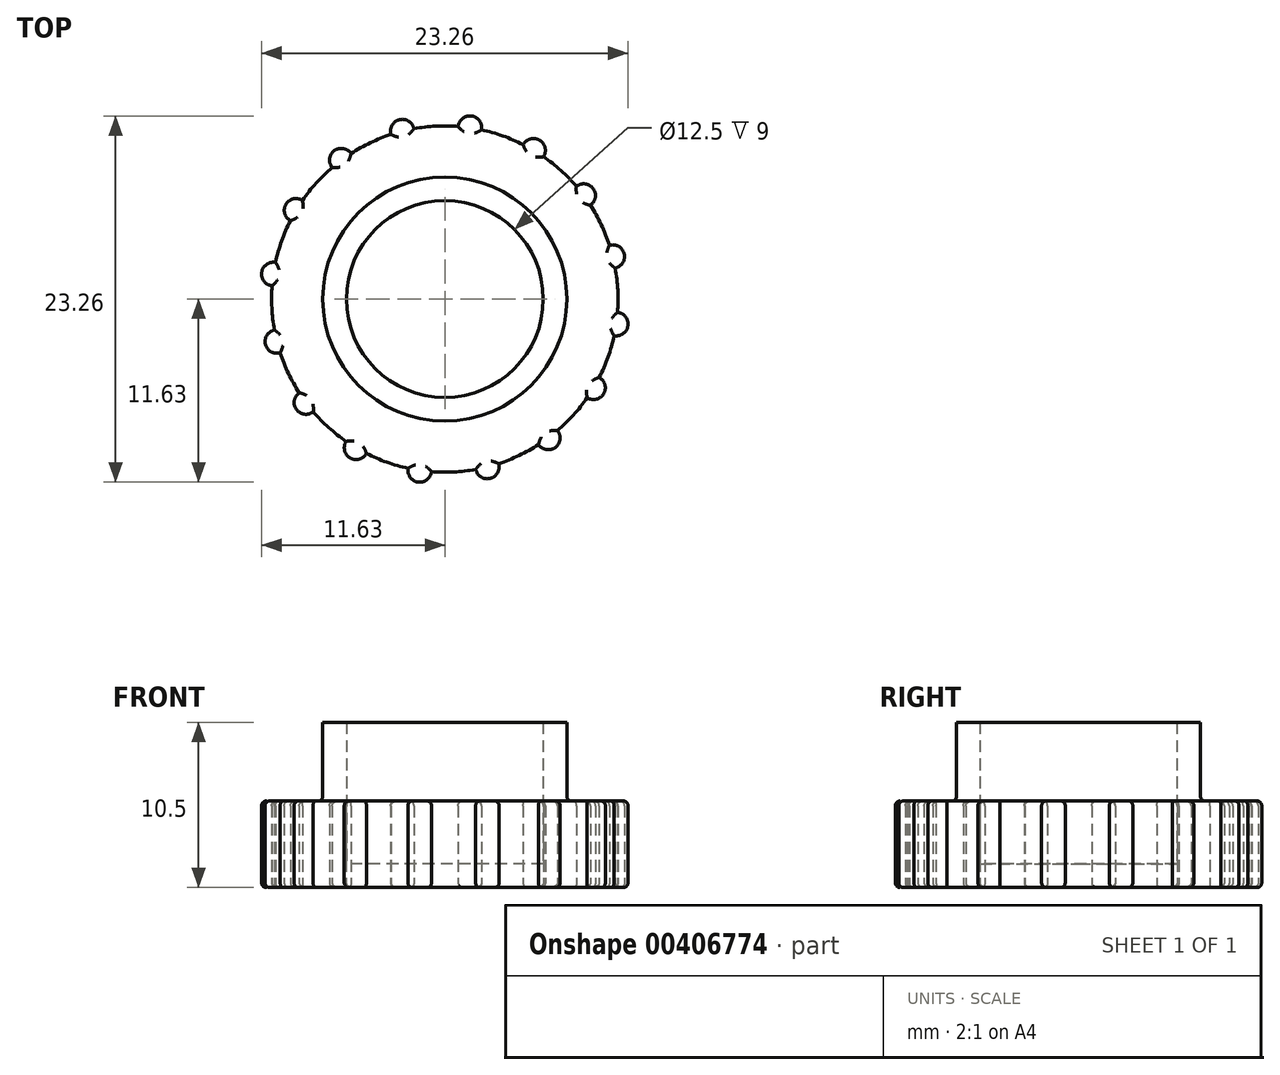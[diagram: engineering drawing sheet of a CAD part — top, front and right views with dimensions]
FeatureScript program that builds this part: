
annotation { "Feature Type Name" : "Feature", "Feature Type Description" : "" }
export const myFeature = defineFeature(function(context is Context, id is Id, definition is map)
    precondition{}
    {
        {
            var Q0;
            Q0=qCreatedBy(makeId("Top.planeOp"),FACE);
            var sketch = newSketch(context, id + "F0", { "sketchPlane" : qUnion([Q0])});
            skCircle(sketch, "E0", {"center": v(0, 0) * mm, "radius": 6.25 * mm});
            skCircle(sketch, "E1", {"center": v(0, 0) * mm, "radius": 7.75 * mm});
            skCircle(sketch, "E2", {"center": v(0, 0) * mm, "radius": 11 * mm});
            skSolve(sketch);
        }
        {
            var Q0;
            Q0=makeQuery(id+"F0.imprint","IMPRINT",FACE,{"disambiguationData":[TD([[makeQuery(id+"F0.imprint","IMPRINT",EDGE,{"derivedFrom":sQuery(id+"F0.wireOp",EDGE,"E0")}),-1.0]])]});
            extrude(context, id + "F1", {"entities" : qUnion([Q0]), "depth" : 9 * mm});
        }
        {
            var Q0;
            Q0=makeQuery(id+"F0.imprint","IMPRINT",FACE,{"disambiguationData":[TD([[makeQuery(id+"F0.imprint","IMPRINT",EDGE,{"derivedFrom":sQuery(id+"F0.wireOp",EDGE,"E1")}),-1.0]])]});
            extrude(context, id + "F2", {"entities" : qUnion([Q0]), "operationType" : NewBodyOperationType.ADD, "depth" : 4 * mm});
        }
        {
            var Q0;
            Q0=makeQuery(id+"F0.imprint","IMPRINT",FACE,{"disambiguationData":[TD([[makeQuery(id+"F0.imprint","IMPRINT",EDGE,{"derivedFrom":sQuery(id+"F0.wireOp",EDGE,"E1")}),-1.0]])]});
            var Q1;
            Q1=makeQuery(id+"F0.imprint","IMPRINT",FACE,{"disambiguationData":[TD([[makeQuery(id+"F0.imprint","IMPRINT",EDGE,{"derivedFrom":sQuery(id+"F0.wireOp",EDGE,"E0")}),-1.0]])]});
            var Q2;
            Q2=makeQuery(id+"F0.imprint","IMPRINT",FACE,{"disambiguationData":[TD([[makeQuery(id+"F0.imprint","IMPRINT",EDGE,{"derivedFrom":sQuery(id+"F0.wireOp",EDGE,"E0")}),1.0]])]});
            extrude(context, id + "F3", {"entities" : qUnion([Q0, Q1, Q2]), "operationType" : NewBodyOperationType.ADD, "oppositeDirection" : true, "depth" : 1.5 * mm});
        }
        {
            var Q0;
            Q0=makeQuery(id+"F3.opExtrude","CAP_FACE",FACE,{"disambiguationData":[OSD([sQuery(id+"F0.wireOp",EDGE,"E2")])],"isStart":false});
            var sketch = newSketch(context, id + "F4", { "sketchPlane" : qUnion([Q0])});
            skCircle(sketch, "E3", {"center": v(-1.6, 10.88) * mm, "radius": 0.75 * mm});
            skSolve(sketch);
        }
        {
            var Q0;
            Q0 = qSketchRegion(id + "F4", true);
            extrude(context, id + "F5", {"entities" : qUnion([Q0]), "oppositeDirection" : true, "depth" : 5.5 * mm});
        }
        {
            var Q0;
            Q0=makeQuery(id+"F5.opExtrude","SWEPT_BODY",BODY,{"disambiguationData":[OSD([sQuery(id+"F4.wireOp",EDGE,"E3")])]});
            var Q1;
            {var subQ0=sQuery(id+"F0.wireOp",EDGE,"E2");Q1=makeQuery(id+"F3.boolean.opBoolean","MERGE",FACE,{"derivedFrom":[makeQuery(id+"F2.opExtrude","SWEPT_FACE",FACE,{"disambiguationData":[OSD([subQ0])]}),makeQuery(id+"F3.opExtrude","SWEPT_FACE",FACE,{"disambiguationData":[OSD([subQ0])]})]});}
            circularPattern(context, id + "F6", {"operationType" : NewBodyOperationType.ADD, "entities" : qUnion([Q0]), "axis" : qUnion([Q1]), "angle" : 360 * degree, "instanceCount" : 16, "equalSpace" : true});
        }
        {
            var Q0;
            Q0=makeQuery(id+"F6.opPattern","COPY",EDGE,{"derivedFrom":makeQuery(id+"F5.opExtrude","CAP_EDGE",EDGE,{"disambiguationData":[OSD([sQuery(id+"F4.wireOp",EDGE,"E3")])],"isStart":true}),"instanceName":"9"});
            var Q1;
            {var subQ0=sQuery(id+"F4.wireOp",EDGE,"E3");var subQ1=makeQuery(id+"F5.opExtrude","CAP_FACE",FACE,{"disambiguationData":[OSD([subQ0])],"isStart":true});var subQ2=sQuery(id+"F0.wireOp",EDGE,"E2");var subQ3=makeQuery(id+"F5.opExtrude","SWEPT_FACE",FACE,{"disambiguationData":[OSD([subQ0])]});Q1=makeQuery(id+"F6.boolean.opBoolean","SPLIT",EDGE,{"disambiguationData":[TD([makeQuery(id+"F2.opExtrude","SWEPT_FACE",FACE,{"disambiguationData":[OSD([subQ2])]}),makeQuery(id+"F3.opExtrude","SWEPT_FACE",FACE,{"disambiguationData":[OSD([subQ2])]}),makeQuery(id+"F3.opExtrude","CAP_FACE",FACE,{"disambiguationData":[OSD([subQ2])],"isStart":false}),subQ1,makeQuery(id+"F6.opPattern","COPY",FACE,{"derivedFrom":subQ1,"instanceName":"1"}),makeQuery(id+"F6.opPattern","COPY",FACE,{"derivedFrom":subQ1,"instanceName":"2"}),makeQuery(id+"F6.opPattern","COPY",FACE,{"derivedFrom":subQ1,"instanceName":"3"}),makeQuery(id+"F6.opPattern","COPY",FACE,{"derivedFrom":subQ1,"instanceName":"4"}),makeQuery(id+"F6.opPattern","COPY",FACE,{"derivedFrom":subQ1,"instanceName":"5"}),makeQuery(id+"F6.opPattern","COPY",FACE,{"derivedFrom":subQ1,"instanceName":"6"}),makeQuery(id+"F6.opPattern","COPY",FACE,{"derivedFrom":subQ1,"instanceName":"7"}),makeQuery(id+"F6.opPattern","COPY",FACE,{"derivedFrom":subQ3,"instanceName":"8"}),makeQuery(id+"F6.opPattern","COPY",FACE,{"derivedFrom":subQ1,"instanceName":"8"}),makeQuery(id+"F6.opPattern","COPY",FACE,{"derivedFrom":subQ3,"instanceName":"9"}),makeQuery(id+"F6.opPattern","COPY",FACE,{"derivedFrom":subQ1,"instanceName":"9"}),makeQuery(id+"F6.opPattern","COPY",FACE,{"derivedFrom":subQ1,"instanceName":"10"}),makeQuery(id+"F6.opPattern","COPY",FACE,{"derivedFrom":subQ1,"instanceName":"11"}),makeQuery(id+"F6.opPattern","COPY",FACE,{"derivedFrom":subQ1,"instanceName":"12"}),makeQuery(id+"F6.opPattern","COPY",FACE,{"derivedFrom":subQ1,"instanceName":"13"}),makeQuery(id+"F6.opPattern","COPY",FACE,{"derivedFrom":subQ1,"instanceName":"14"}),makeQuery(id+"F6.opPattern","COPY",FACE,{"derivedFrom":subQ1,"instanceName":"15"})])],"derivedFrom":makeQuery(id+"F3.opExtrude","CAP_EDGE",EDGE,{"disambiguationData":[OSD([subQ2])],"isStart":false})});}
            var Q2;
            Q2=makeQuery(id+"F6.opPattern","COPY",EDGE,{"derivedFrom":makeQuery(id+"F5.opExtrude","CAP_EDGE",EDGE,{"disambiguationData":[OSD([sQuery(id+"F4.wireOp",EDGE,"E3")])],"isStart":true}),"instanceName":"8"});
            var Q3;
            {var subQ0=sQuery(id+"F4.wireOp",EDGE,"E3");var subQ1=makeQuery(id+"F5.opExtrude","CAP_FACE",FACE,{"disambiguationData":[OSD([subQ0])],"isStart":true});var subQ2=sQuery(id+"F0.wireOp",EDGE,"E2");var subQ3=makeQuery(id+"F5.opExtrude","SWEPT_FACE",FACE,{"disambiguationData":[OSD([subQ0])]});Q3=makeQuery(id+"F6.boolean.opBoolean","SPLIT",EDGE,{"disambiguationData":[TD([makeQuery(id+"F2.opExtrude","SWEPT_FACE",FACE,{"disambiguationData":[OSD([subQ2])]}),makeQuery(id+"F3.opExtrude","SWEPT_FACE",FACE,{"disambiguationData":[OSD([subQ2])]}),makeQuery(id+"F3.opExtrude","CAP_FACE",FACE,{"disambiguationData":[OSD([subQ2])],"isStart":false}),subQ1,makeQuery(id+"F6.opPattern","COPY",FACE,{"derivedFrom":subQ1,"instanceName":"1"}),makeQuery(id+"F6.opPattern","COPY",FACE,{"derivedFrom":subQ1,"instanceName":"2"}),makeQuery(id+"F6.opPattern","COPY",FACE,{"derivedFrom":subQ1,"instanceName":"3"}),makeQuery(id+"F6.opPattern","COPY",FACE,{"derivedFrom":subQ1,"instanceName":"4"}),makeQuery(id+"F6.opPattern","COPY",FACE,{"derivedFrom":subQ1,"instanceName":"5"}),makeQuery(id+"F6.opPattern","COPY",FACE,{"derivedFrom":subQ1,"instanceName":"6"}),makeQuery(id+"F6.opPattern","COPY",FACE,{"derivedFrom":subQ3,"instanceName":"7"}),makeQuery(id+"F6.opPattern","COPY",FACE,{"derivedFrom":subQ1,"instanceName":"7"}),makeQuery(id+"F6.opPattern","COPY",FACE,{"derivedFrom":subQ3,"instanceName":"8"}),makeQuery(id+"F6.opPattern","COPY",FACE,{"derivedFrom":subQ1,"instanceName":"8"}),makeQuery(id+"F6.opPattern","COPY",FACE,{"derivedFrom":subQ1,"instanceName":"9"}),makeQuery(id+"F6.opPattern","COPY",FACE,{"derivedFrom":subQ1,"instanceName":"10"}),makeQuery(id+"F6.opPattern","COPY",FACE,{"derivedFrom":subQ1,"instanceName":"11"}),makeQuery(id+"F6.opPattern","COPY",FACE,{"derivedFrom":subQ1,"instanceName":"12"}),makeQuery(id+"F6.opPattern","COPY",FACE,{"derivedFrom":subQ1,"instanceName":"13"}),makeQuery(id+"F6.opPattern","COPY",FACE,{"derivedFrom":subQ1,"instanceName":"14"}),makeQuery(id+"F6.opPattern","COPY",FACE,{"derivedFrom":subQ1,"instanceName":"15"})])],"derivedFrom":makeQuery(id+"F3.opExtrude","CAP_EDGE",EDGE,{"disambiguationData":[OSD([subQ2])],"isStart":false})});}
            var Q4;
            Q4=makeQuery(id+"F6.opPattern","COPY",EDGE,{"derivedFrom":makeQuery(id+"F5.opExtrude","CAP_EDGE",EDGE,{"disambiguationData":[OSD([sQuery(id+"F4.wireOp",EDGE,"E3")])],"isStart":true}),"instanceName":"7"});
            var Q5;
            {var subQ0=sQuery(id+"F4.wireOp",EDGE,"E3");var subQ1=makeQuery(id+"F5.opExtrude","CAP_FACE",FACE,{"disambiguationData":[OSD([subQ0])],"isStart":true});var subQ2=sQuery(id+"F0.wireOp",EDGE,"E2");var subQ3=makeQuery(id+"F5.opExtrude","SWEPT_FACE",FACE,{"disambiguationData":[OSD([subQ0])]});Q5=makeQuery(id+"F6.boolean.opBoolean","SPLIT",EDGE,{"disambiguationData":[TD([makeQuery(id+"F2.opExtrude","SWEPT_FACE",FACE,{"disambiguationData":[OSD([subQ2])]}),makeQuery(id+"F3.opExtrude","SWEPT_FACE",FACE,{"disambiguationData":[OSD([subQ2])]}),makeQuery(id+"F3.opExtrude","CAP_FACE",FACE,{"disambiguationData":[OSD([subQ2])],"isStart":false}),subQ1,makeQuery(id+"F6.opPattern","COPY",FACE,{"derivedFrom":subQ1,"instanceName":"1"}),makeQuery(id+"F6.opPattern","COPY",FACE,{"derivedFrom":subQ1,"instanceName":"2"}),makeQuery(id+"F6.opPattern","COPY",FACE,{"derivedFrom":subQ1,"instanceName":"3"}),makeQuery(id+"F6.opPattern","COPY",FACE,{"derivedFrom":subQ1,"instanceName":"4"}),makeQuery(id+"F6.opPattern","COPY",FACE,{"derivedFrom":subQ1,"instanceName":"5"}),makeQuery(id+"F6.opPattern","COPY",FACE,{"derivedFrom":subQ3,"instanceName":"6"}),makeQuery(id+"F6.opPattern","COPY",FACE,{"derivedFrom":subQ1,"instanceName":"6"}),makeQuery(id+"F6.opPattern","COPY",FACE,{"derivedFrom":subQ3,"instanceName":"7"}),makeQuery(id+"F6.opPattern","COPY",FACE,{"derivedFrom":subQ1,"instanceName":"7"}),makeQuery(id+"F6.opPattern","COPY",FACE,{"derivedFrom":subQ1,"instanceName":"8"}),makeQuery(id+"F6.opPattern","COPY",FACE,{"derivedFrom":subQ1,"instanceName":"9"}),makeQuery(id+"F6.opPattern","COPY",FACE,{"derivedFrom":subQ1,"instanceName":"10"}),makeQuery(id+"F6.opPattern","COPY",FACE,{"derivedFrom":subQ1,"instanceName":"11"}),makeQuery(id+"F6.opPattern","COPY",FACE,{"derivedFrom":subQ1,"instanceName":"12"}),makeQuery(id+"F6.opPattern","COPY",FACE,{"derivedFrom":subQ1,"instanceName":"13"}),makeQuery(id+"F6.opPattern","COPY",FACE,{"derivedFrom":subQ1,"instanceName":"14"}),makeQuery(id+"F6.opPattern","COPY",FACE,{"derivedFrom":subQ1,"instanceName":"15"})])],"derivedFrom":makeQuery(id+"F3.opExtrude","CAP_EDGE",EDGE,{"disambiguationData":[OSD([subQ2])],"isStart":false})});}
            var Q6;
            Q6=makeQuery(id+"F6.opPattern","COPY",EDGE,{"derivedFrom":makeQuery(id+"F5.opExtrude","CAP_EDGE",EDGE,{"disambiguationData":[OSD([sQuery(id+"F4.wireOp",EDGE,"E3")])],"isStart":true}),"instanceName":"6"});
            var Q7;
            {var subQ0=sQuery(id+"F4.wireOp",EDGE,"E3");var subQ1=makeQuery(id+"F5.opExtrude","CAP_FACE",FACE,{"disambiguationData":[OSD([subQ0])],"isStart":true});var subQ2=makeQuery(id+"F5.opExtrude","SWEPT_FACE",FACE,{"disambiguationData":[OSD([subQ0])]});var subQ3=sQuery(id+"F0.wireOp",EDGE,"E2");Q7=makeQuery(id+"F6.boolean.opBoolean","SPLIT",EDGE,{"disambiguationData":[TD([makeQuery(id+"F2.opExtrude","SWEPT_FACE",FACE,{"disambiguationData":[OSD([subQ3])]}),makeQuery(id+"F3.opExtrude","SWEPT_FACE",FACE,{"disambiguationData":[OSD([subQ3])]}),makeQuery(id+"F3.opExtrude","CAP_FACE",FACE,{"disambiguationData":[OSD([subQ3])],"isStart":false}),subQ1,makeQuery(id+"F6.opPattern","COPY",FACE,{"derivedFrom":subQ1,"instanceName":"1"}),makeQuery(id+"F6.opPattern","COPY",FACE,{"derivedFrom":subQ1,"instanceName":"2"}),makeQuery(id+"F6.opPattern","COPY",FACE,{"derivedFrom":subQ1,"instanceName":"3"}),makeQuery(id+"F6.opPattern","COPY",FACE,{"derivedFrom":subQ1,"instanceName":"4"}),makeQuery(id+"F6.opPattern","COPY",FACE,{"derivedFrom":subQ2,"instanceName":"5"}),makeQuery(id+"F6.opPattern","COPY",FACE,{"derivedFrom":subQ1,"instanceName":"5"}),makeQuery(id+"F6.opPattern","COPY",FACE,{"derivedFrom":subQ2,"instanceName":"6"}),makeQuery(id+"F6.opPattern","COPY",FACE,{"derivedFrom":subQ1,"instanceName":"6"}),makeQuery(id+"F6.opPattern","COPY",FACE,{"derivedFrom":subQ1,"instanceName":"7"}),makeQuery(id+"F6.opPattern","COPY",FACE,{"derivedFrom":subQ1,"instanceName":"8"}),makeQuery(id+"F6.opPattern","COPY",FACE,{"derivedFrom":subQ1,"instanceName":"9"}),makeQuery(id+"F6.opPattern","COPY",FACE,{"derivedFrom":subQ1,"instanceName":"10"}),makeQuery(id+"F6.opPattern","COPY",FACE,{"derivedFrom":subQ1,"instanceName":"11"}),makeQuery(id+"F6.opPattern","COPY",FACE,{"derivedFrom":subQ1,"instanceName":"12"}),makeQuery(id+"F6.opPattern","COPY",FACE,{"derivedFrom":subQ1,"instanceName":"13"}),makeQuery(id+"F6.opPattern","COPY",FACE,{"derivedFrom":subQ1,"instanceName":"14"}),makeQuery(id+"F6.opPattern","COPY",FACE,{"derivedFrom":subQ1,"instanceName":"15"})])],"derivedFrom":makeQuery(id+"F3.opExtrude","CAP_EDGE",EDGE,{"disambiguationData":[OSD([subQ3])],"isStart":false})});}
            var Q8;
            Q8=makeQuery(id+"F6.opPattern","COPY",EDGE,{"derivedFrom":makeQuery(id+"F5.opExtrude","CAP_EDGE",EDGE,{"disambiguationData":[OSD([sQuery(id+"F4.wireOp",EDGE,"E3")])],"isStart":true}),"instanceName":"5"});
            var Q9;
            {var subQ0=sQuery(id+"F4.wireOp",EDGE,"E3");var subQ1=makeQuery(id+"F5.opExtrude","CAP_FACE",FACE,{"disambiguationData":[OSD([subQ0])],"isStart":true});var subQ2=makeQuery(id+"F5.opExtrude","SWEPT_FACE",FACE,{"disambiguationData":[OSD([subQ0])]});var subQ3=sQuery(id+"F0.wireOp",EDGE,"E2");Q9=makeQuery(id+"F6.boolean.opBoolean","SPLIT",EDGE,{"disambiguationData":[TD([makeQuery(id+"F2.opExtrude","SWEPT_FACE",FACE,{"disambiguationData":[OSD([subQ3])]}),makeQuery(id+"F3.opExtrude","SWEPT_FACE",FACE,{"disambiguationData":[OSD([subQ3])]}),makeQuery(id+"F3.opExtrude","CAP_FACE",FACE,{"disambiguationData":[OSD([subQ3])],"isStart":false}),subQ1,makeQuery(id+"F6.opPattern","COPY",FACE,{"derivedFrom":subQ1,"instanceName":"1"}),makeQuery(id+"F6.opPattern","COPY",FACE,{"derivedFrom":subQ1,"instanceName":"2"}),makeQuery(id+"F6.opPattern","COPY",FACE,{"derivedFrom":subQ1,"instanceName":"3"}),makeQuery(id+"F6.opPattern","COPY",FACE,{"derivedFrom":subQ2,"instanceName":"4"}),makeQuery(id+"F6.opPattern","COPY",FACE,{"derivedFrom":subQ1,"instanceName":"4"}),makeQuery(id+"F6.opPattern","COPY",FACE,{"derivedFrom":subQ2,"instanceName":"5"}),makeQuery(id+"F6.opPattern","COPY",FACE,{"derivedFrom":subQ1,"instanceName":"5"}),makeQuery(id+"F6.opPattern","COPY",FACE,{"derivedFrom":subQ1,"instanceName":"6"}),makeQuery(id+"F6.opPattern","COPY",FACE,{"derivedFrom":subQ1,"instanceName":"7"}),makeQuery(id+"F6.opPattern","COPY",FACE,{"derivedFrom":subQ1,"instanceName":"8"}),makeQuery(id+"F6.opPattern","COPY",FACE,{"derivedFrom":subQ1,"instanceName":"9"}),makeQuery(id+"F6.opPattern","COPY",FACE,{"derivedFrom":subQ1,"instanceName":"10"}),makeQuery(id+"F6.opPattern","COPY",FACE,{"derivedFrom":subQ1,"instanceName":"11"}),makeQuery(id+"F6.opPattern","COPY",FACE,{"derivedFrom":subQ1,"instanceName":"12"}),makeQuery(id+"F6.opPattern","COPY",FACE,{"derivedFrom":subQ1,"instanceName":"13"}),makeQuery(id+"F6.opPattern","COPY",FACE,{"derivedFrom":subQ1,"instanceName":"14"}),makeQuery(id+"F6.opPattern","COPY",FACE,{"derivedFrom":subQ1,"instanceName":"15"})])],"derivedFrom":makeQuery(id+"F3.opExtrude","CAP_EDGE",EDGE,{"disambiguationData":[OSD([subQ3])],"isStart":false})});}
            var Q10;
            {var subQ0=makeQuery(id+"F5.opExtrude","CAP_FACE",FACE,{"disambiguationData":[OSD([sQuery(id+"F4.wireOp",EDGE,"E3")])],"isStart":true});Q10=makeQuery(id+"F6.boolean.opBoolean","MERGE",FACE,{"derivedFrom":[makeQuery(id+"F3.opExtrude","CAP_FACE",FACE,{"disambiguationData":[OSD([sQuery(id+"F0.wireOp",EDGE,"E2")])],"isStart":false}),subQ0,makeQuery(id+"F6.opPattern","COPY",FACE,{"derivedFrom":subQ0,"instanceName":"1"}),makeQuery(id+"F6.opPattern","COPY",FACE,{"derivedFrom":subQ0,"instanceName":"2"}),makeQuery(id+"F6.opPattern","COPY",FACE,{"derivedFrom":subQ0,"instanceName":"3"}),makeQuery(id+"F6.opPattern","COPY",FACE,{"derivedFrom":subQ0,"instanceName":"4"}),makeQuery(id+"F6.opPattern","COPY",FACE,{"derivedFrom":subQ0,"instanceName":"5"}),makeQuery(id+"F6.opPattern","COPY",FACE,{"derivedFrom":subQ0,"instanceName":"6"}),makeQuery(id+"F6.opPattern","COPY",FACE,{"derivedFrom":subQ0,"instanceName":"7"}),makeQuery(id+"F6.opPattern","COPY",FACE,{"derivedFrom":subQ0,"instanceName":"8"}),makeQuery(id+"F6.opPattern","COPY",FACE,{"derivedFrom":subQ0,"instanceName":"9"}),makeQuery(id+"F6.opPattern","COPY",FACE,{"derivedFrom":subQ0,"instanceName":"10"}),makeQuery(id+"F6.opPattern","COPY",FACE,{"derivedFrom":subQ0,"instanceName":"11"}),makeQuery(id+"F6.opPattern","COPY",FACE,{"derivedFrom":subQ0,"instanceName":"12"}),makeQuery(id+"F6.opPattern","COPY",FACE,{"derivedFrom":subQ0,"instanceName":"13"}),makeQuery(id+"F6.opPattern","COPY",FACE,{"derivedFrom":subQ0,"instanceName":"14"}),makeQuery(id+"F6.opPattern","COPY",FACE,{"derivedFrom":subQ0,"instanceName":"15"})]});}
            fillet(context, id + "F7", {"entities" : qUnion([Q0, Q1, Q2, Q3, Q4, Q5, Q6, Q7, Q8, Q9, Q10]), "radius" : 0.3 * mm, "tangentPropagation" : true, "allowEdgeOverflow" : false});
        }
        {
            var Q0;
            {var subQ0=makeQuery(id+"F5.opExtrude","CAP_FACE",FACE,{"disambiguationData":[OSD([sQuery(id+"F4.wireOp",EDGE,"E3")])],"isStart":false});Q0=makeQuery(id+"F6.boolean.opBoolean","MERGE",FACE,{"derivedFrom":[makeQuery(id+"F2.opExtrude","CAP_FACE",FACE,{"disambiguationData":[OSD([sQuery(id+"F0.wireOp",EDGE,"E1"),sQuery(id+"F0.wireOp",EDGE,"E2")])],"isStart":false}),subQ0,makeQuery(id+"F6.opPattern","COPY",FACE,{"derivedFrom":subQ0,"instanceName":"1"}),makeQuery(id+"F6.opPattern","COPY",FACE,{"derivedFrom":subQ0,"instanceName":"2"}),makeQuery(id+"F6.opPattern","COPY",FACE,{"derivedFrom":subQ0,"instanceName":"3"}),makeQuery(id+"F6.opPattern","COPY",FACE,{"derivedFrom":subQ0,"instanceName":"4"}),makeQuery(id+"F6.opPattern","COPY",FACE,{"derivedFrom":subQ0,"instanceName":"5"}),makeQuery(id+"F6.opPattern","COPY",FACE,{"derivedFrom":subQ0,"instanceName":"6"}),makeQuery(id+"F6.opPattern","COPY",FACE,{"derivedFrom":subQ0,"instanceName":"7"}),makeQuery(id+"F6.opPattern","COPY",FACE,{"derivedFrom":subQ0,"instanceName":"8"}),makeQuery(id+"F6.opPattern","COPY",FACE,{"derivedFrom":subQ0,"instanceName":"9"}),makeQuery(id+"F6.opPattern","COPY",FACE,{"derivedFrom":subQ0,"instanceName":"10"}),makeQuery(id+"F6.opPattern","COPY",FACE,{"derivedFrom":subQ0,"instanceName":"11"}),makeQuery(id+"F6.opPattern","COPY",FACE,{"derivedFrom":subQ0,"instanceName":"12"}),makeQuery(id+"F6.opPattern","COPY",FACE,{"derivedFrom":subQ0,"instanceName":"13"}),makeQuery(id+"F6.opPattern","COPY",FACE,{"derivedFrom":subQ0,"instanceName":"14"}),makeQuery(id+"F6.opPattern","COPY",FACE,{"derivedFrom":subQ0,"instanceName":"15"})]});}
            fillet(context, id + "F8", {"entities" : qUnion([Q0]), "radius" : 0.3 * mm, "tangentPropagation" : true, "allowEdgeOverflow" : false});
        }
    });
